# Revit family: НЕВАТОМ_Вентилятор VO фланцевое, версия 1
name_source: partatom
category: Оборудование
revit_build: Autodesk Revit 2017 (Build: 20170118_1100(x64)
units: mm (PartAtom-declared; Revit-internal decimal feet)

## family parameters
Всегда вертикально = Да
На основе рабочей плоскости = Нет
Общий = Нет
При загрузке вырезать с полостями = Нет
Размер круглого соединителя = Использовать диаметр
Тип детали = Нормальный
Точка расчета площади = Нет

## types (14) — shared parameters
ADSK_Единица измерения = шт.
ADSK_Завод-изготовитель = НЕВАТОМ
ADSK_Количество = 1
ADSK_Материал наименование = Оцинкованная сталь
ADSK_Наименование = Вентилятор осевой
Nevatom_URL = https://t.me

## per-type parameters (varying)
| type | ADSK_Марка | ADSK_Масса | ADSK_Масса_Текст | ADSK_Напряжение | ADSK_Полная мощность | ADSK_Размер_Высота | ADSK_Размер_Длина | ADSK_Размер_Ширина | ADSK_Ток | ADSK_Частота вращения вентилятора | B | D | D верх вент | D осн вент | D* | D1 | D1.1 | D2 | D2.1 | H | А | С |
| VO 200-4E | VO 200-4Е-01 | 1.9 | 1.9 кг | 230 В | 0 кВт | 250 мм | 250 мм | 180 мм | 0 А | 1460 | 250 мм | 208 мм | 26 мм | 42 мм | 17 мм | 194 мм | 153 мм | 139 мм | 97 мм | 126 мм | 230 мм | 180 мм |
| VO 250-4E | VO 250-4Е-01 | 2.5 | 2.5 кг | 230 В | 0 кВт | 310 мм | 310 мм | 180 мм | 0 А | 1380 | 310 мм | 260 мм | 33 мм | 52 мм | 22 мм | 243 мм | 191 мм | 173 мм | 121 мм | 134 мм | 285 мм | 180 мм |
| VO 300-4Е | VO 300-4Е-01 | 3.2 | 3.2 кг | 230 В | 0 кВт | 382 мм | 382 мм | 180 мм | 0 А | 1370 | 382 мм | 310 мм | 39 мм | 62 мм | 26 мм | 289 мм | 227 мм | 207 мм | 145 мм | 158 мм | 356 мм | 180 мм |
| VO 350-4Е | VO 350-4Е-01 | 4.7 | 4.7 кг | 230 В | 0 кВт | 421 мм | 421 мм | 180 мм | 1 А | 1370 | 421 мм | 359 мм | 45 мм | 72 мм | 30 мм | 335 мм | 263 мм | 239 мм | 168 мм | 158 мм | 395 мм | 180 мм |
| VO 400-4Е | VO 400-4Е-01 | 6.1 | 6.1 кг | 230 В | 0 кВт | 465 мм | 465 мм | 190 мм | 1 А | 1350 | 465 мм | 400 мм | 50 мм | 80 мм | 33 мм | 373 мм | 293 мм | 267 мм | 187 мм | 171 мм | 438 мм | 190 мм |
| VO 450-4E | VO 450-4Е-01 | 6.9 | 6.9 кг | 230 В | 0 кВт | 515 мм | 515 мм | 190 мм | 1 А | 1380 | 515 мм | 460 мм | 58 мм | 92 мм | 38 мм | 429 мм | 337 мм | 307 мм | 215 мм | 183 мм | 487 мм | 190 мм |
| VO 400-4D | VO 400-4D-01 | 6.1 | 6.1 кг | 380 В | 0 кВт | 465 мм | 465 мм | 190 мм | 0 А | 1380 | 465 мм | 400 мм | 50 мм | 80 мм | 33 мм | 373 мм | 293 мм | 267 мм | 187 мм | 171 мм | 438 мм | 190 мм |
| VO 450-4D | VO 450-4D-01 | 6.9 | 6.9 кг | 380 В | 0 кВт | 515 мм | 515 мм | 190 мм | 1 А | 1400 | 515 мм | 460 мм | 58 мм | 92 мм | 38 мм | 429 мм | 337 мм | 307 мм | 215 мм | 183 мм | 487 мм | 190 мм |
| VO 500-4E | VO 500-4E-01 | 9.5 | 9.5 кг | 230 В | 0 кВт | 567 мм | 567 мм | 250 мм | 2 А | 1320 | 567 мм | 513 мм | 64 мм | 103 мм | 43 мм | 479 мм | 376 мм | 342 мм | 239 мм | 186 мм | 541 мм | 250 мм |
| VO 500-4D | VO 500-4D-01 | 9.5 | 9.5 кг | 380 В | 0 кВт | 567 мм | 567 мм | 250 мм | 1 А | 1320 | 567 мм | 513 мм | 64 мм | 103 мм | 43 мм | 479 мм | 376 мм | 342 мм | 239 мм | 186 мм | 541 мм | 250 мм |
| VO 560-4E | VO 560-4E-01 | 10.5 | 10.5 кг | 230 В | 1 кВт | 635 мм | 635 мм | 250 мм | 2 А | 1310 | 635 мм | 565 мм | 71 мм | 113 мм | 47 мм | 527 мм | 414 мм | 377 мм | 264 мм | 201 мм | 605 мм | 250 мм |
| VO 560-4D | VO 560-4D-01 | 10.5 | 10.5 кг | 380 В | 1 кВт | 635 мм | 635 мм | 250 мм | 1 А | 1300 | 635 мм | 565 мм | 71 мм | 113 мм | 47 мм | 527 мм | 414 мм | 377 мм | 264 мм | 201 мм | 605 мм | 250 мм |
| VO 630-4E | VO 630-4E-01 | 15 | 15.0 кг | 230 В | 1 кВт | 707 мм | 707 мм | 250 мм | 4 А | 1315 | 707 мм | 643 мм | 80 мм | 129 мм | 54 мм | 600 мм | 472 мм | 429 мм | 300 мм | 221 мм | 674 мм | 250 мм |
| VO 630-4D | VO 630-6D-01 | 15 | 15.0 кг | 380 В | 1 кВт | 707 мм | 707 мм | 250 мм | 2 А | 1365 | 707 мм | 643 мм | 80 мм | 129 мм | 54 мм | 600 мм | 472 мм | 429 мм | 300 мм | 221 мм | 674 мм | 250 мм |
